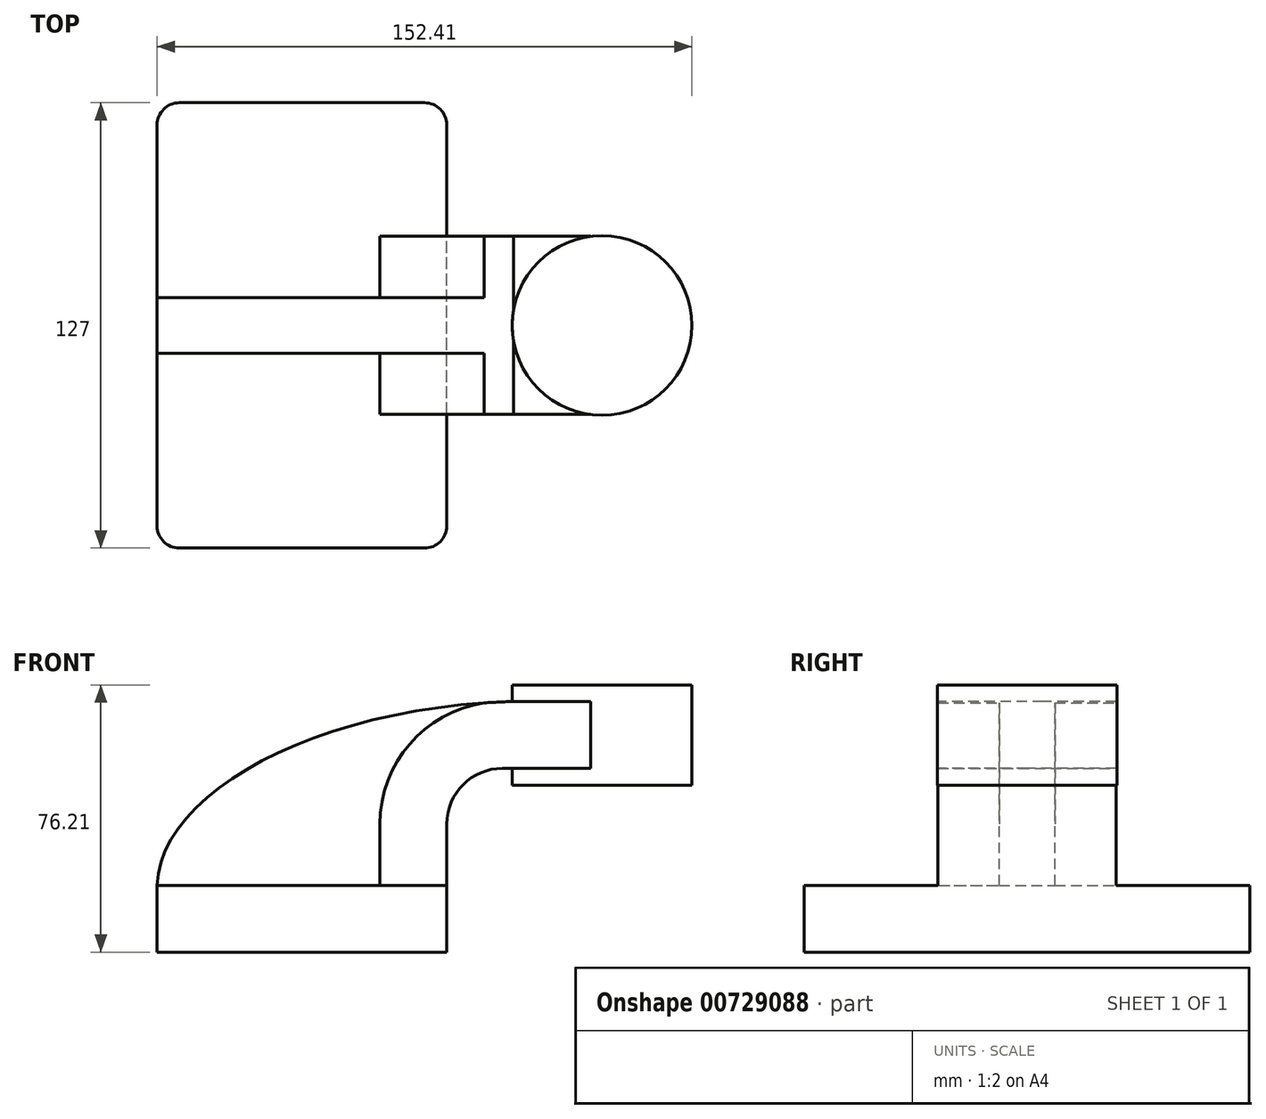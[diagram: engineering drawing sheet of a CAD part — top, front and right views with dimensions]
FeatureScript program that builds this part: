
annotation { "Feature Type Name" : "Feature", "Feature Type Description" : "" }
export const myFeature = defineFeature(function(context is Context, id is Id, definition is map)
    precondition{}
    {
        {
            var Q0;
            Q0=qCreatedBy(makeId("Front.planeOp"),FACE);
            var sketch = newSketch(context, id + "F0", { "sketchPlane" : qUnion([Q0])});
            skLineSegment(sketch, "E0.bottom", {"start": v(41.28, -9.52) * mm, "end": v(-41.28, -9.53) * mm});
            skLineSegment(sketch, "E0.top", {"start": v(41.28, 9.53) * mm, "end": v(-41.28, 9.53) * mm});
            skLineSegment(sketch, "E0.left", {"start": v(41.28, -9.52) * mm, "end": v(41.28, 9.53) * mm});
            skLineSegment(sketch, "E0.right", {"start": v(-41.28, -9.52) * mm, "end": v(-41.28, 9.53) * mm});
            skPoint(sketch, "E0.middle", {"position": v(0, 0) * mm});
            skLineSegment(sketch, "E1.bottom", {"start": v(111.12, 38.1) * mm, "end": v(60.32, 38.1) * mm});
            skLineSegment(sketch, "E1.top", {"start": v(111.12, 66.68) * mm, "end": v(60.32, 66.68) * mm});
            skLineSegment(sketch, "E1.left", {"start": v(111.12, 38.1) * mm, "end": v(111.12, 66.68) * mm});
            skLineSegment(sketch, "E1.right", {"start": v(60.32, 38.1) * mm, "end": v(60.32, 66.68) * mm});
            skPoint(sketch, "E1.middle", {"position": v(85.72, 52.39) * mm});
            skLineSegment(sketch, "E2", {"start": v(41.28, 9.53) * mm, "end": v(41.28, 27) * mm});
            skArc(sketch, "E3", {"start": v(41.27, 27) * mm, "mid": v(45.92, 38.23) * mm, "end": v(57.15, 42.88) * mm});
            skLineSegment(sketch, "E4", {"start": v(57.15, 42.88) * mm, "end": v(85.52, 42.88) * mm});
            skLineSegment(sketch, "E5.0", {"start": v(57.15, 61.93) * mm, "end": v(85.52, 61.93) * mm});
            skArc(sketch, "E5.1", {"start": v(22.23, 27) * mm, "mid": v(32.45, 51.7) * mm, "end": v(57.15, 61.93) * mm});
            skLineSegment(sketch, "E5.2", {"start": v(22.22, 9.53) * mm, "end": v(22.22, 27) * mm});
            skLineSegment(sketch, "E6", {"start": v(85.52, 38.1) * mm, "end": v(85.52, 66.68) * mm});
            skPoint(sketch, "E6.endSnap0", {"position": v(85.72, 66.68) * mm});
            skFitSpline(sketch, "E7", {"points": [v(-41.28, 9.52) * mm, v(60.32, 61.93) * mm], "startDerivative": vector(2.61, 80.38) * mm, "endDerivative": vector(166, 4.18) * mm});
            skSolve(sketch);
        }
        {
            var Q0;
            Q0=makeQuery(id+"F0.imprint","IMPRINT",FACE,{"disambiguationData":[TD([[makeQuery(id+"F0.imprint","IMPRINT",EDGE,{"derivedFrom":sQuery(id+"F0.wireOp",EDGE,"E0.bottom")}),-1.0]])]});
            extrude(context, id + "F1", {"entities" : qUnion([Q0]), "surfaceOperationType" : NewSurfaceOperationType.ADD, "endBound" : BoundingType.SYMMETRIC, "depth" : 127 * mm, "offsetDistance" : 25.4 * mm});
        }
        {
            var Q0;
            {var subQ3=sQuery(id+"F0.wireOp",EDGE,"E5.2");Q0=makeQuery(id+"F0.imprint","IMPRINT",FACE,{"disambiguationData":[TD([[makeQuery(id+"F0.imprint","IMPRINT",EDGE,{"derivedFrom":subQ3}),1.0]])]});}
            extrude(context, id + "F2", {"entities" : qUnion([Q0]), "operationType" : NewBodyOperationType.ADD, "endBound" : BoundingType.SYMMETRIC, "depth" : 15.88 * mm, "offsetDistance" : 25.4 * mm});
        }
        {
            var Q0;
            Q0=makeQuery(id+"F1.opExtrude","CAP_EDGE",EDGE,{"disambiguationData":[OSD([sQuery(id+"F0.wireOp",EDGE,"E0.left")])],"isStart":false});
            var Q1;
            Q1=makeQuery(id+"F1.opExtrude","CAP_EDGE",EDGE,{"disambiguationData":[OSD([sQuery(id+"F0.wireOp",EDGE,"E0.right")])],"isStart":false});
            var Q2;
            Q2=makeQuery(id+"F1.opExtrude","CAP_EDGE",EDGE,{"disambiguationData":[OSD([sQuery(id+"F0.wireOp",EDGE,"E0.left")])],"isStart":true});
            var Q3;
            Q3=makeQuery(id+"F1.opExtrude","CAP_EDGE",EDGE,{"disambiguationData":[OSD([sQuery(id+"F0.wireOp",EDGE,"E0.right")])],"isStart":true});
            fillet(context, id + "F3", {"entities" : qUnion([Q0, Q1, Q2, Q3]), "radius" : 6.35 * mm, "tangentPropagation" : true, "allowEdgeOverflow" : false});
        }
        {
            var Q0;
            {var subQ1=sQuery(id+"F0.wireOp",EDGE,"E2");Q0=makeQuery(id+"F0.imprint","IMPRINT",FACE,{"disambiguationData":[TD([[makeQuery(id+"F0.imprint","IMPRINT",EDGE,{"derivedFrom":subQ1}),1.0]])]});}
            var Q1;
            {var subQ3=sQuery(id+"F0.wireOp",EDGE,"E4");var subQ5=sQuery(id+"F0.wireOp",EDGE,"E6");var subQ6=makeQuery(id+"F0.imprint","INTERSECT",VERTEX,{"derivedFrom":[subQ3,subQ5]});Q1=makeQuery(id+"F0.imprint","IMPRINT",FACE,{"disambiguationData":[TD([[makeQuery(id+"F0.imprint","IMPRINT",EDGE,{"disambiguationData":[TD([[subQ6,1.0]])],"derivedFrom":subQ3}),1.0]])]});}
            extrude(context, id + "F4", {"entities" : qUnion([Q0, Q1]), "operationType" : NewBodyOperationType.ADD, "endBound" : BoundingType.SYMMETRIC, "depth" : 50.8 * mm, "offsetDistance" : 25.4 * mm});
        }
        {
            var Q0;
            {var subQ0=sQuery(id+"F0.wireOp",EDGE,"E1.left");Q0=makeQuery(id+"F0.imprint","IMPRINT",FACE,{"disambiguationData":[TD([[makeQuery(id+"F0.imprint","IMPRINT",EDGE,{"derivedFrom":subQ0}),1.0]])]});}
            var Q1;
            Q1=sQuery(id+"F0.wireOp",EDGE,"E6");
            revolve(context, id + "F5", {"operationType" : NewBodyOperationType.ADD, "surfaceOperationType" : NewSurfaceOperationType.NEW, "entities" : qUnion([Q0]), "axis" : qUnion([Q1]), "revolveType" : RevolveType.FULL});
        }
    });
